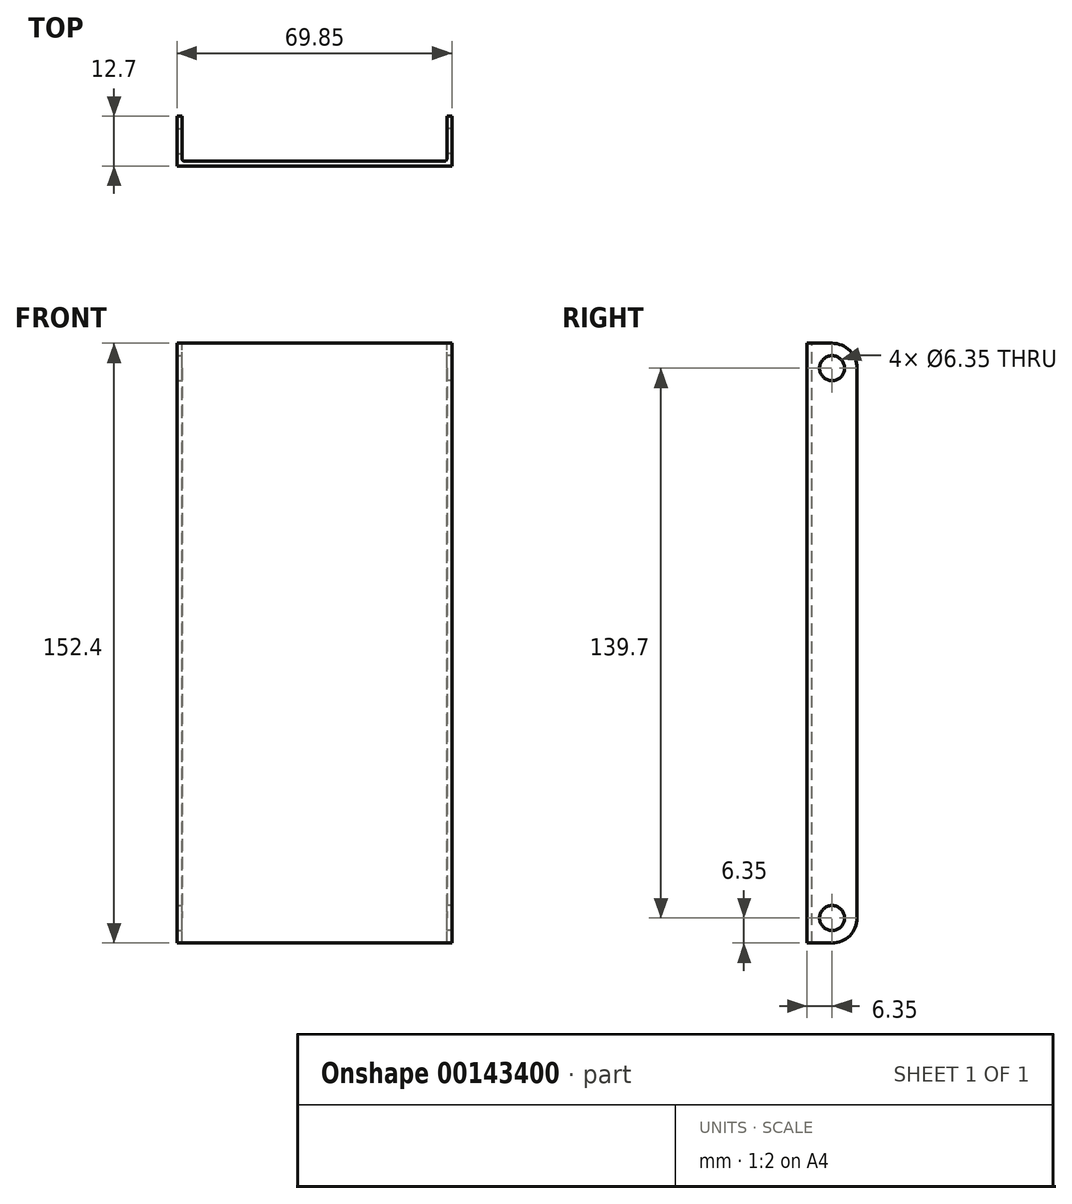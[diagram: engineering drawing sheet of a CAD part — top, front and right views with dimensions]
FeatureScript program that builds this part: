
annotation { "Feature Type Name" : "Feature", "Feature Type Description" : "" }
export const myFeature = defineFeature(function(context is Context, id is Id, definition is map)
    precondition{}
    {
        {
            var Q0;
            Q0=qCreatedBy(makeId("Right.planeOp"),FACE);
            var sketch = newSketch(context, id + "F0", { "sketchPlane" : qUnion([Q0])});
            skLineSegment(sketch, "E0.bottom", {"start": v(0, 0) * mm, "end": v(6.35, 0) * mm});
            skLineSegment(sketch, "E0.top", {"start": v(0, -76.2) * mm, "end": v(12.7, -76.2) * mm});
            skLineSegment(sketch, "E0.left", {"start": v(0, 0) * mm, "end": v(0, -76.2) * mm});
            skLineSegment(sketch, "E0.right", {"start": v(12.7, -6.35) * mm, "end": v(12.7, -76.2) * mm});
            skPoint(sketch, "E1.visualSharp", {"position": v(12.7, 0) * mm});
            skArc(sketch, "E1.filletArc", {"start": v(12.7, -6.35) * mm, "mid": v(10.84, -1.86) * mm, "end": v(6.35, 0) * mm});
            skCircle(sketch, "E2", {"center": v(6.35, -6.35) * mm, "radius": 3.18 * mm});
            skLineSegment(sketch, "E3.MirrorCS", {"start": v(12.7, -146.05) * mm, "end": v(12.7, -76.2) * mm});
            skLineSegment(sketch, "E4.MirrorCS", {"start": v(0, -152.4) * mm, "end": v(6.35, -152.4) * mm});
            skLineSegment(sketch, "E5.MirrorCS", {"start": v(0, -152.4) * mm, "end": v(0, -76.2) * mm});
            skArc(sketch, "E6.MirrorCS", {"start": v(12.7, -146.05) * mm, "mid": v(10.84, -150.54) * mm, "end": v(6.35, -152.4) * mm});
            skCircle(sketch, "E7.MirrorC", {"center": v(6.35, -146.05) * mm, "radius": 3.18 * mm});
            skSolve(sketch);
        }
        {
            var Q0;
            Q0=makeQuery(id+"F0.imprint","IMPRINT",FACE,{"disambiguationData":[TD([[makeQuery(id+"F0.imprint","IMPRINT",EDGE,{"derivedFrom":sQuery(id+"F0.wireOp",EDGE,"E0.bottom")}),-1.0]])]});
            var Q1;
            Q1=makeQuery(id+"F0.imprint","IMPRINT",FACE,{"disambiguationData":[TD([[makeQuery(id+"F0.imprint","IMPRINT",EDGE,{"derivedFrom":sQuery(id+"F0.wireOp",EDGE,"E0.top")}),-1.0]])]});
            extrude(context, id + "F1", {"entities" : qUnion([Q0, Q1]), "depth" : 1.27 * mm});
        }
        {
            var Q0;
            Q0=makeQuery(id+"F1.opExtrude","SWEPT_FACE",FACE,{"disambiguationData":[OSD([sQuery(id+"F0.wireOp",EDGE,"E0.bottom")])]});
            var sketch = newSketch(context, id + "F2", { "sketchPlane" : qUnion([Q0])});
            skArc(sketch, "E8", {"start": v(-0.64, 1.27) * mm, "mid": v(-0.19, 1.46) * mm, "end": v(0, 1.9) * mm});
            skLineSegment(sketch, "E9.0", {"start": v(0, 0) * mm, "end": v(0, 6.35) * mm});
            skLineSegment(sketch, "E10", {"start": v(-0.64, 1.27) * mm, "end": v(-33.66, 1.27) * mm});
            skLineSegment(sketch, "E11", {"start": v(-33.66, 1.27) * mm, "end": v(-33.66, 0) * mm});
            skLineSegment(sketch, "E12", {"start": v(-33.66, 0) * mm, "end": v(0, 0) * mm});
            skSolve(sketch);
        }
        {
            var Q0;
            {var subQ2=sQuery(id+"F2.wireOp",EDGE,"E8");Q0=makeQuery(id+"F2.imprint","IMPRINT",FACE,{"disambiguationData":[TD([[makeQuery(id+"F2.imprint","IMPRINT",EDGE,{"derivedFrom":subQ2}),-1.0]])]});}
            var Q1;
            Q1=makeQuery(id+"F1.opExtrude","SWEPT_FACE",FACE,{"disambiguationData":[OSD([sQuery(id+"F0.wireOp",EDGE,"E4.MirrorCS")])]});
            extrude(context, id + "F3", {"entities" : qUnion([Q0]), "operationType" : NewBodyOperationType.ADD, "endBound" : BoundingType.UP_TO_SURFACE, "oppositeDirection" : true, "endBoundEntityFace" : qUnion([Q1]), "depth" : 25.4 * mm});
        }
        {
            var Q0;
            Q0=makeQuery(id+"F1.opExtrude","SWEPT_BODY",BODY,{"disambiguationData":[OSD([sQuery(id+"F0.wireOp",EDGE,"E0.bottom"),sQuery(id+"F0.wireOp",EDGE,"E0.left"),sQuery(id+"F0.wireOp",EDGE,"E0.right"),sQuery(id+"F0.wireOp",EDGE,"E1.filletArc"),sQuery(id+"F0.wireOp",EDGE,"E2"),sQuery(id+"F0.wireOp",EDGE,"E3.MirrorCS"),sQuery(id+"F0.wireOp",EDGE,"E4.MirrorCS"),sQuery(id+"F0.wireOp",EDGE,"E5.MirrorCS"),sQuery(id+"F0.wireOp",EDGE,"E6.MirrorCS"),sQuery(id+"F0.wireOp",EDGE,"E7.MirrorC")])]});
            var Q1;
            Q1=makeQuery(id+"F3.opExtrude","SWEPT_FACE",FACE,{"disambiguationData":[OSD([sQuery(id+"F2.wireOp",EDGE,"E11")])]});
            mirror(context, id + "F4", {"operationType" : NewBodyOperationType.ADD, "entities" : qUnion([Q0]), "mirrorPlane" : qUnion([Q1])});
        }
    });
